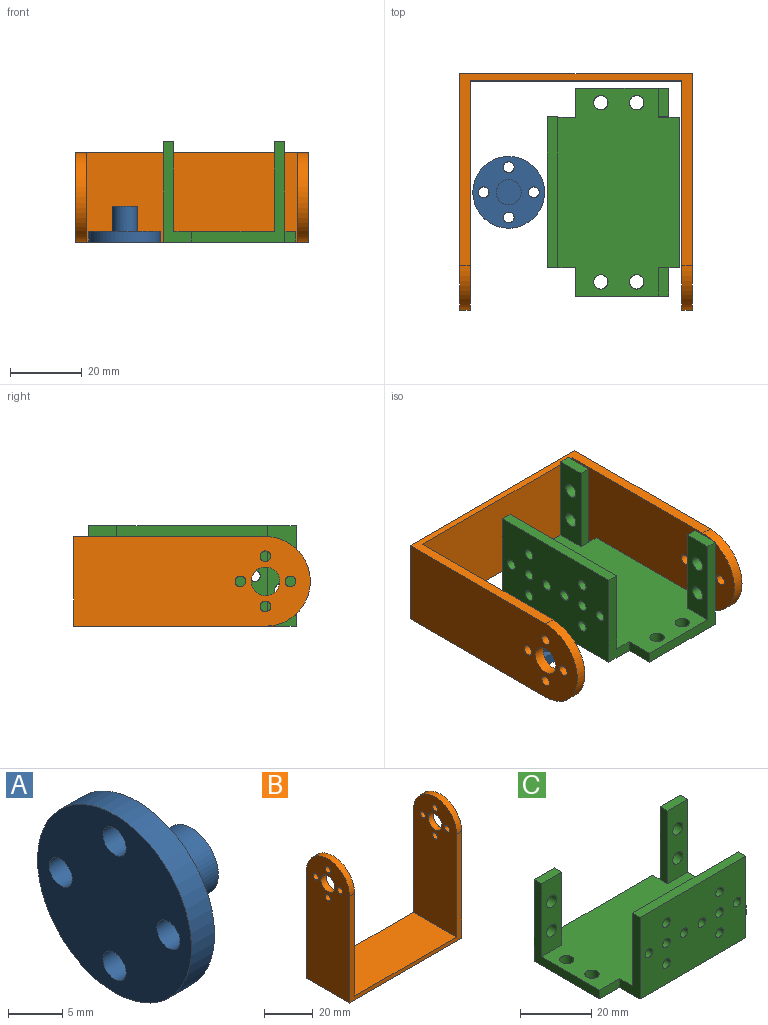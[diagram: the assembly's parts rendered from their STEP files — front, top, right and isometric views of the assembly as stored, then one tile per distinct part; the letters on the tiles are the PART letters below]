
ASSEMBLY  parts=3 mates=2
PART A: 9 faces, bbox 10x20x20 mm
  f0: cylinder r=1.5mm len=3mm, axis (-1,0,0), area 28.3mm2, adj f5,f6
  f1: cylinder r=1.5mm len=3mm, axis (-1,0,0), area 28.3mm2, adj f5,f6
  f2: cylinder r=1.5mm len=3mm, axis (-1,0,0), area 28.3mm2, adj f5,f6
  f3: cylinder r=1.5mm len=3mm, axis (-1,0,0), area 28.3mm2, adj f5,f6
  f4: cylinder r=10mm len=20mm, axis (-1,0,0), area 188.5mm2, adj f5,f6
  f5: plane 20x20mm, normal (1,0,0), area 247.4mm2, adj f0,f1,f2,f3,f4,f7
  f6: plane 20x20mm, normal (-1,0,0), area 285.9mm2, adj f0,f1,f2,f3,f4
  f7: cylinder r=3.5mm len=7mm, axis (-1,0,0), area 153.9mm2, adj f5,f8
  f8: plane 7x7mm, normal (1,0,0), area 38.5mm2, adj f7
PART B: 20 faces, bbox 65x25x66 mm
  f0: plane 66x25mm, normal (-1,0,0), area 1504.4mm2, adj f5,f6,f7,f9,f15,f16,f17,f18
  f1: plane 66x25mm, normal (1,0,0), area 1504.4mm2, adj f5,f6,f7,f8,f10,f11,f12,f13
  f2: plane 64x25mm, normal (1,0,0), area 1454.4mm2, adj f4,f5,f6,f9,f15,f16,f17,f18
  f3: plane 64x25mm, normal (-1,0,0), area 1454.4mm2, adj f4,f5,f6,f8,f10,f11,f12,f13
  f4: plane 59x25mm, normal (0,0,1), area 1475mm2, adj f2,f3,f5,f6
  f5: plane 65x53.5mm, normal (0,-1,0), area 439mm2, adj f0,f1,f2,f3,f4,f7,f8,f9
  f6: plane 65x53.5mm, normal (0,1,0), area 439mm2, adj f0,f1,f2,f3,f4,f7,f8,f9
  f7: plane 65x25mm, normal (0,0,-1), area 1625mm2, adj f0,f1,f5,f6
  f8: cylinder r=12.5mm len=25mm, axis (-1,0,0), area 117.8mm2, adj f1,f3,f5,f6
  f9: cylinder r=12.5mm len=25mm, axis (-1,0,0), area 117.8mm2, adj f0,f2,f5,f6
  f10: cylinder r=1.5mm len=3mm, axis (-1,0,0), area 28.3mm2, adj f1,f3
  f11: cylinder r=1.5mm len=3mm, axis (-1,0,0), area 28.3mm2, adj f1,f3
  f12: cylinder r=4mm len=8mm, axis (-1,0,0), area 75.4mm2, adj f1,f3
  f13: cylinder r=1.5mm len=3mm, axis (-1,0,0), area 28.3mm2, adj f1,f3
  f14: cylinder r=1.5mm len=3mm, axis (-1,0,0), area 28.3mm2, adj f1,f3
  f15: cylinder r=1.5mm len=3mm, axis (-1,0,0), area 28.3mm2, adj f0,f2
  f16: cylinder r=1.5mm len=3mm, axis (-1,0,0), area 28.3mm2, adj f0,f2
  f17: cylinder r=4mm len=8mm, axis (-1,0,0), area 75.4mm2, adj f0,f2
  f18: cylinder r=1.5mm len=3mm, axis (-1,0,0), area 28.3mm2, adj f0,f2
  f19: cylinder r=1.5mm len=3mm, axis (-1,0,0), area 28.3mm2, adj f0,f2
PART C: 40 faces, bbox 58x37x28 mm
  f0: plane 58x34mm, normal (0,0,1), area 1745.7mm2, adj f1,f2,f3,f5,f6,f7,f9,f10
  f1: plane 28x26mm, normal (-1,0,0), area 153mm2, adj f0,f2,f12,f13,f16,f18
  f2: plane 8x3mm, normal (0,-1,0), area 24mm2, adj f0,f1,f3,f13
  f3: plane 28x8mm, normal (-1,0,0), area 99mm2, adj f0,f2,f4,f13,f14,f15
  f4: plane 42x28mm, normal (0,-1,0), area 1105.3mm2, adj f3,f5,f13,f15,f26,f27,f28,f29
  f5: plane 28x8mm, normal (1,0,0), area 99mm2, adj f0,f4,f6,f13,f14,f15
  f6: plane 8x3mm, normal (0,-1,0), area 24mm2, adj f0,f5,f7,f13
  f7: plane 28x26mm, normal (1,0,0), area 153mm2, adj f0,f6,f8,f13,f19,f21
  f8: plane 28x8mm, normal (0,1,0), area 198.9mm2, adj f7,f9,f13,f20,f21,f22,f23
  f9: plane 3x3mm, normal (1,0,0), area 9mm2, adj f0,f8,f10,f13
  f10: plane 42x3mm, normal (0,1,0), area 126mm2, adj f0,f9,f11,f13
  f11: plane 3x3mm, normal (-1,0,0), area 9mm2, adj f0,f10,f12,f13
  f12: plane 28x8mm, normal (0,1,0), area 198.9mm2, adj f1,f11,f13,f17,f18,f24,f25
  f13: plane 58x37mm, normal (0,0,-1), area 1919.7mm2, adj f1,f2,f3,f4,f5,f6,f7,f8
  f14: plane 42x25mm, normal (0,1,0), area 979.3mm2, adj f0,f3,f5,f15,f26,f27,f28,f29
  f15: plane 42x3mm, normal (0,0,1), area 126mm2, adj f3,f4,f5,f14
  f16: plane 25x8mm, normal (0,-1,0), area 174.9mm2, adj f0,f1,f17,f18,f24,f25
  f17: plane 25x3mm, normal (1,0,0), area 75mm2, adj f0,f12,f16,f18
  f18: plane 8x3mm, normal (0,0,1), area 24mm2, adj f1,f12,f16,f17
  f19: plane 25x8mm, normal (0,-1,0), area 174.9mm2, adj f0,f7,f20,f21,f22,f23
  f20: plane 25x3mm, normal (-1,0,0), area 75mm2, adj f0,f8,f19,f21
  f21: plane 8x3mm, normal (0,0,1), area 24mm2, adj f7,f8,f19,f20
  f22: cylinder r=2mm len=4mm, axis (0,-1,0), area 37.7mm2, adj f8,f19
  f23: cylinder r=2mm len=4mm, axis (0,-1,0), area 37.7mm2, adj f8,f19
  f24: cylinder r=2mm len=4mm, axis (0,-1,0), area 37.7mm2, adj f12,f16
  f25: cylinder r=2mm len=4mm, axis (0,-1,0), area 37.7mm2, adj f12,f16
  f26: cylinder r=1.5mm len=3mm, axis (0,-1,0), area 28.3mm2, adj f4,f14
  f27: cylinder r=1.5mm len=3mm, axis (0,-1,0), area 28.3mm2, adj f4,f14
  f28: cylinder r=1.5mm len=3mm, axis (0,-1,0), area 28.3mm2, adj f4,f14
  f29: cylinder r=1.5mm len=3mm, axis (0,-1,0), area 28.3mm2, adj f4,f14
  f30: cylinder r=1.5mm len=3mm, axis (0,-1,0), area 28.3mm2, adj f4,f14
  f31: cylinder r=1.5mm len=3mm, axis (0,-1,0), area 28.3mm2, adj f4,f14
  f32: cylinder r=1.5mm len=3mm, axis (0,-1,0), area 28.3mm2, adj f4,f14
  f33: cylinder r=1.5mm len=3mm, axis (0,-1,0), area 28.3mm2, adj f4,f14
  f34: cylinder r=1.5mm len=3mm, axis (0,-1,0), area 28.3mm2, adj f4,f14
  f35: cylinder r=1.5mm len=3mm, axis (0,-1,0), area 28.3mm2, adj f4,f14
  f36: cylinder r=2mm len=4mm, axis (0,0,-1), area 37.7mm2, adj f0,f13
  f37: cylinder r=2mm len=4mm, axis (0,0,-1), area 37.7mm2, adj f0,f13
  f38: cylinder r=2mm len=4mm, axis (0,0,-1), area 37.7mm2, adj f0,f13
  f39: cylinder r=2mm len=4mm, axis (0,0,-1), area 37.7mm2, adj f0,f13
PLACE A rot(axis=(0,-1,0),90deg) t=(-18.77,4.61,38.51)mm
PLACE B rot(axis=(1,0,0),90deg) t=(-32.5,37.66,38.51)mm
PLACE C rot(axis=(0,0,-1),90deg) t=(-8.07,33.61,38.51)mm
MATE planar A.f4 <-> C.f13  axis (0,0,-1) through (-18.77,4.61,38.51)mm
MATE planar C.f13 <-> B.f5  axis (0,0,-1) through (10.93,4.61,38.51)mm
